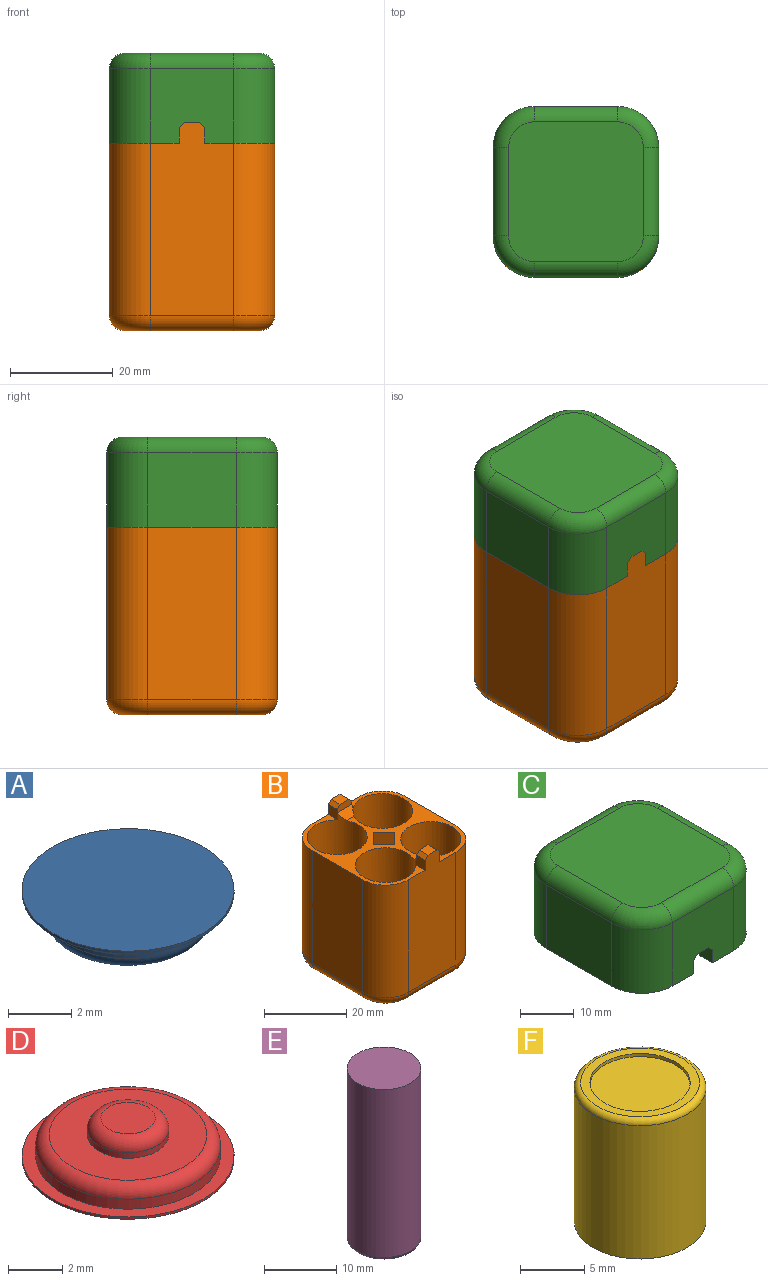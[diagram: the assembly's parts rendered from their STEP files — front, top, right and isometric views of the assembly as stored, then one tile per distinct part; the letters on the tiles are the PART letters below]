
ASSEMBLY  parts=6 mates=5
PART A: 7 faces, bbox 7.7x7.7x1.3 mm
  f0: cylinder r=3.35mm len=6.7mm, axis (0,0,1), area 2.1mm2, adj f1,f2
  f1: plane 6.7x6.7mm, normal (0,0,-1), area 3.1mm2, adj f0,f5
  f2: plane 6.7x6.7mm, normal (0,0,1), area 35.3mm2, adj f0
  f3: cylinder r=2.7mm len=5.4mm, axis (0,0,1), area 2.5mm2, adj f5,f6
  f4: plane 4.4x4.4mm, normal (0,0,-1), area 15.2mm2, adj f6
  f5: torus R=3.2mm, axis (0,0,-1), area 14.2mm2, adj f1,f3
  f6: torus R=2.2mm, axis (0,0,-1), area 12.4mm2, adj f3,f4
PART B: 45 faces, bbox 33.5x34.5x40.5 mm
  f0: plane 33.2x32.2mm, normal (0,0,1), area 273mm2, adj f1,f2,f3,f4,f5,f6,f7,f8
  f1: plane 33.5x17.2mm, normal (-1,0,0), area 576.2mm2, adj f0,f2,f12,f26
  f2: cylinder r=8mm len=33.5mm, axis (0,0,-1), area 421mm2, adj f0,f1,f3,f28
  f3: plane 37.5x16.2mm, normal (0,-1,0), area 561.7mm2, adj f0,f2,f4,f30,f32,f33,f34,f41
  f4: cylinder r=8mm len=33.5mm, axis (0,0,-1), area 421mm2, adj f0,f3,f5,f29
  f5: plane 33.5x17.2mm, normal (1,0,0), area 576.2mm2, adj f0,f4,f6,f27
  f6: cylinder r=8mm len=33.5mm, axis (0,0,-1), area 421mm2, adj f0,f5,f7,f25
  f7: plane 37.5x16.2mm, normal (0,1,0), area 561.7mm2, adj f0,f6,f12,f23,f36,f37,f38,f39
  f8: cylinder r=7.3mm len=36.72mm, axis (0,0,-1), area 1607.2mm2, adj f0,f13,f37,f43
  f9: cylinder r=7.3mm len=36.72mm, axis (0,0,-1), area 1607.2mm2, adj f0,f14,f36,f43
  f10: cylinder r=7.3mm len=36.72mm, axis (0,0,-1), area 1607.2mm2, adj f0,f15,f32,f44
  f11: cylinder r=7.3mm len=36.72mm, axis (0,0,-1), area 1607.2mm2, adj f0,f16,f33,f44
  f12: cylinder r=8mm len=33.5mm, axis (0,0,-1), area 421mm2, adj f0,f1,f7,f24
  f13: plane 14.6x14.6mm, normal (0,0,1), area 167.4mm2, adj f8
  f14: plane 14.6x14.6mm, normal (0,0,1), area 167.4mm2, adj f9
  f15: plane 14.6x14.6mm, normal (0,0,1), area 167.4mm2, adj f10
  f16: plane 14.6x14.6mm, normal (0,0,1), area 167.4mm2, adj f11
  f17: plane 27.2x26.2mm, normal (0,0,-1), area 691.2mm2, adj f23,f24,f25,f26,f27,f28,f29,f30
  f18: plane 5.5x3.61mm, normal (-0.71,-0.71,0), area 28.1mm2, adj f0,f19,f21,f22
  f19: plane 5.5x3.61mm, normal (0.71,-0.71,0), area 28.1mm2, adj f0,f18,f20,f22
  f20: plane 5.5x3.61mm, normal (0.71,0.71,0), area 28.1mm2, adj f0,f19,f21,f22
  f21: plane 5.5x3.61mm, normal (-0.71,0.71,0), area 28.1mm2, adj f0,f18,f20,f22
  f22: plane 7.21x7.21mm, normal (0,0,1), area 26mm2, adj f18,f19,f20,f21
  f23: cylinder r=3mm len=16.2mm, axis (1,0,0), area 76.3mm2, adj f7,f17,f24,f25
  f24: torus R=5mm, axis (0,0,-1), area 51.1mm2, adj f12,f17,f23,f26
  f25: torus R=5mm, axis (0,0,-1), area 51.1mm2, adj f6,f17,f23,f27
  f26: cylinder r=3mm len=17.2mm, axis (0,1,0), area 81.1mm2, adj f1,f17,f24,f28
  f27: cylinder r=3mm len=17.2mm, axis (0,-1,0), area 81.1mm2, adj f5,f17,f25,f29
  f28: torus R=5mm, axis (0,0,-1), area 51.1mm2, adj f2,f17,f26,f30
  f29: torus R=5mm, axis (0,0,-1), area 51.1mm2, adj f4,f17,f27,f30
  f30: cylinder r=3mm len=16.2mm, axis (-1,0,0), area 76.3mm2, adj f3,f17,f28,f29
  f31: plane 5x2mm, normal (0,1,0), area 9mm2, adj f32,f33,f34,f41,f42,f44
  f32: plane 3.28x3mm, normal (-1,0,0), area 9.5mm2, adj f0,f3,f10,f31,f41,f44
  f33: plane 3.28x3mm, normal (1,0,0), area 9.5mm2, adj f0,f3,f11,f31,f42,f44
  f34: plane 3x3mm, normal (0,0,1), area 9mm2, adj f3,f31,f41,f42
  f35: plane 5x2mm, normal (0,-1,0), area 9mm2, adj f36,f37,f38,f39,f40,f43
  f36: plane 3.28x3mm, normal (1,0,0), area 9.5mm2, adj f0,f7,f9,f35,f40,f43
  f37: plane 3.28x3mm, normal (-1,0,0), area 9.5mm2, adj f0,f7,f8,f35,f39,f43
  f38: plane 3x3mm, normal (0,0,1), area 9mm2, adj f7,f35,f39,f40
  f39: plane 3x1mm, normal (-0.71,0,0.71), area 4.2mm2, adj f7,f35,f37,f38
  f40: plane 3x1mm, normal (0.71,0,0.71), area 4.2mm2, adj f7,f35,f36,f38
  f41: plane 3x1mm, normal (-0.71,0,0.71), area 4.2mm2, adj f3,f31,f32,f34
  f42: plane 3x1mm, normal (0.71,0,0.71), area 4.2mm2, adj f3,f31,f33,f34
  f43: plane 5x2mm, normal (0,-0.71,0.71), area 10.9mm2, adj f0,f8,f9,f35,f36,f37
  f44: plane 5x2mm, normal (0,0.71,0.71), area 10.9mm2, adj f0,f10,f11,f31,f32,f33
PART C: 45 faces, bbox 33.5x34.5x17.5 mm
  f0: plane 16.2x14.5mm, normal (0,1,0), area 215.9mm2, adj f1,f2,f8,f26,f32,f33,f34,f35
  f1: plane 33.2x32.2mm, normal (0,0,-1), area 273mm2, adj f0,f2,f3,f4,f5,f6,f7,f8
  f2: cylinder r=8mm len=14.5mm, axis (0,0,-1), area 182.2mm2, adj f0,f1,f3,f24
  f3: plane 17.2x14.5mm, normal (-1,0,0), area 249.4mm2, adj f1,f2,f4,f23
  f4: cylinder r=8mm len=14.5mm, axis (0,0,-1), area 182.2mm2, adj f1,f3,f5,f25
  f5: plane 16.2x14.5mm, normal (0,-1,0), area 215.9mm2, adj f1,f4,f6,f27,f39,f40,f41,f42
  f6: cylinder r=8mm len=14.5mm, axis (0,0,-1), area 182.2mm2, adj f1,f5,f7,f29
  f7: plane 17.2x14.5mm, normal (1,0,0), area 249.4mm2, adj f1,f6,f8,f30
  f8: cylinder r=8mm len=14.5mm, axis (0,0,-1), area 182.2mm2, adj f0,f1,f7,f28
  f9: cylinder r=7.3mm len=16mm, axis (0,0,-1), area 732mm2, adj f1,f13,f36,f37
  f10: cylinder r=7.3mm len=16mm, axis (0,0,-1), area 732mm2, adj f1,f14,f35,f37
  f11: cylinder r=7.3mm len=16mm, axis (0,0,-1), area 732mm2, adj f1,f15,f39,f44
  f12: cylinder r=7.3mm len=16mm, axis (0,0,-1), area 732mm2, adj f1,f16,f40,f44
  f13: plane 14.6x14.6mm, normal (0,0,-1), area 167.4mm2, adj f9
  f14: plane 14.6x14.6mm, normal (0,0,-1), area 167.4mm2, adj f10
  f15: plane 14.6x14.6mm, normal (0,0,-1), area 167.4mm2, adj f11
  f16: plane 14.6x14.6mm, normal (0,0,-1), area 167.4mm2, adj f12
  f17: plane 27.2x26.2mm, normal (0,0,1), area 691.2mm2, adj f23,f24,f25,f26,f27,f28,f29,f30
  f18: plane 5.5x3.61mm, normal (0.71,-0.71,0), area 28.1mm2, adj f1,f19,f21,f22
  f19: plane 5.5x3.61mm, normal (-0.71,-0.71,0), area 28.1mm2, adj f1,f18,f20,f22
  f20: plane 5.5x3.61mm, normal (-0.71,0.71,0), area 28.1mm2, adj f1,f19,f21,f22
  f21: plane 5.5x3.61mm, normal (0.71,0.71,0), area 28.1mm2, adj f1,f18,f20,f22
  f22: plane 7.21x7.21mm, normal (0,0,-1), area 26mm2, adj f18,f19,f20,f21
  f23: cylinder r=3mm len=17.2mm, axis (0,1,0), area 81.1mm2, adj f3,f17,f24,f25
  f24: torus R=5mm, axis (0,0,1), area 51.1mm2, adj f2,f17,f23,f26
  f25: torus R=5mm, axis (0,0,1), area 51.1mm2, adj f4,f17,f23,f27
  f26: cylinder r=3mm len=16.2mm, axis (1,0,0), area 76.3mm2, adj f0,f17,f24,f28
  f27: cylinder r=3mm len=16.2mm, axis (-1,0,0), area 76.3mm2, adj f5,f17,f25,f29
  f28: torus R=5mm, axis (0,0,1), area 51.1mm2, adj f8,f17,f26,f30
  f29: torus R=5mm, axis (0,0,1), area 51.1mm2, adj f6,f17,f27,f30
  f30: cylinder r=3mm len=17.2mm, axis (0,-1,0), area 81.1mm2, adj f7,f17,f28,f29
  f31: plane 5x2mm, normal (0,1,0), area 9mm2, adj f32,f33,f34,f35,f36,f37
  f32: plane 3x1mm, normal (-0.71,0,-0.71), area 4.2mm2, adj f0,f31,f34,f35
  f33: plane 3x1mm, normal (0.71,0,-0.71), area 4.2mm2, adj f0,f31,f34,f36
  f34: plane 3x3mm, normal (0,0,-1), area 9mm2, adj f0,f31,f32,f33
  f35: plane 3.28x3mm, normal (-1,0,0), area 9.5mm2, adj f0,f1,f10,f31,f32,f37
  f36: plane 3.28x3mm, normal (1,0,0), area 9.5mm2, adj f0,f1,f9,f31,f33,f37
  f37: plane 5x2mm, normal (0,0.71,-0.71), area 10.9mm2, adj f1,f9,f10,f31,f35,f36
  f38: plane 5x2mm, normal (0,-1,0), area 9mm2, adj f39,f40,f41,f42,f43,f44
  f39: plane 3.28x3mm, normal (1,0,0), area 9.5mm2, adj f1,f5,f11,f38,f42,f44
  f40: plane 3.28x3mm, normal (-1,0,0), area 9.5mm2, adj f1,f5,f12,f38,f43,f44
  f41: plane 3x3mm, normal (0,0,-1), area 9mm2, adj f5,f38,f42,f43
  f42: plane 3x1mm, normal (0.71,0,-0.71), area 4.2mm2, adj f5,f38,f39,f41
  f43: plane 3x1mm, normal (-0.71,0,-0.71), area 4.2mm2, adj f5,f38,f40,f41
  f44: plane 5x2mm, normal (0,-0.71,-0.71), area 10.9mm2, adj f1,f11,f12,f38,f39,f40
PART D: 9 faces, bbox 7.8x7.8x1.8 mm
  f0: cylinder r=3.9mm len=7.8mm, axis (0,0,-1), area 2.5mm2, adj f1,f2
  f1: plane 7.8x7.8mm, normal (0,0,1), area 11.5mm2, adj f0,f3
  f2: plane 7.8x7.8mm, normal (0,0,-1), area 47.8mm2, adj f0
  f3: cylinder r=3.4mm len=6.8mm, axis (0,0,-1), area 9.6mm2, adj f1,f8
  f4: plane 5.8x5.8mm, normal (0,0,1), area 19.4mm2, adj f5,f8
  f5: cylinder r=1.5mm len=3mm, axis (0,0,-1), area 2.4mm2, adj f4,f7
  f6: plane 2x2mm, normal (0,0,1), area 3.1mm2, adj f7
  f7: torus R=1mm, axis (0,0,1), area 6.5mm2, adj f5,f6
  f8: torus R=2.9mm, axis (0,0,1), area 15.9mm2, adj f3,f4
PART E: 6 faces, bbox 11.1x11.1x29 mm
  f0: cylinder r=5.12mm len=28.5mm, axis (0,0,-1), area 917.7mm2, adj f1,f5
  f1: plane 10.25x10.25mm, normal (0,0,1), area 82.5mm2, adj f0
  f2: plane 9.25x9.25mm, normal (0,0,-1), area 31.9mm2, adj f3,f5
  f3: cylinder r=3.35mm len=6.7mm, axis (0,0,-1), area 12.6mm2, adj f2,f4
  f4: plane 6.7x6.7mm, normal (0,0,-1), area 35.3mm2, adj f3
  f5: torus R=4.62mm, axis (0,0,1), area 24.4mm2, adj f0,f2
PART F: 6 faces, bbox 11.1x11.1x13.2 mm
  f0: cylinder r=5.12mm len=12.7mm, axis (0,0,-1), area 409mm2, adj f2,f5
  f1: plane 9.25x9.25mm, normal (0,0,1), area 19.4mm2, adj f3,f5
  f2: plane 10.25x10.25mm, normal (0,0,-1), area 82.5mm2, adj f0
  f3: cylinder r=3.9mm len=7.8mm, axis (0,0,1), area 7.4mm2, adj f1,f4
  f4: plane 7.8x7.8mm, normal (0,0,1), area 47.8mm2, adj f3
  f5: torus R=4.62mm, axis (0,0,1), area 24.4mm2, adj f0,f1
PLACE A t=(-6.07,10.28,-10.46)mm
PLACE B t=(-13.87,18.58,-11.11)mm fixed
PLACE C t=(-13.87,18.58,-11.11)mm
PLACE D t=(-6.07,10.28,-10.36)mm
PLACE E t=(-6.07,10.28,-10.36)mm
PLACE F t=(-6.07,10.28,-10.36)mm
MATE fastened A.f3 <-> B.f11  axis (0,0,-1) through (-6.07,10.28,-11.11)mm
MATE fastened D.f0 <-> F.f3  axis (0,0,-1) through (-6.07,10.28,31.54)mm
MATE slider B.f0 <-> C.f1  axis (0,0,1) through (-13.87,18.58,23.89)mm
MATE fastened E.f0 <-> F.f0  axis (0,0,1) through (-6.07,10.28,18.64)mm
MATE fastened E.f0 <-> A.f0  axis (0,0,-1) through (-6.07,10.28,-9.86)mm
